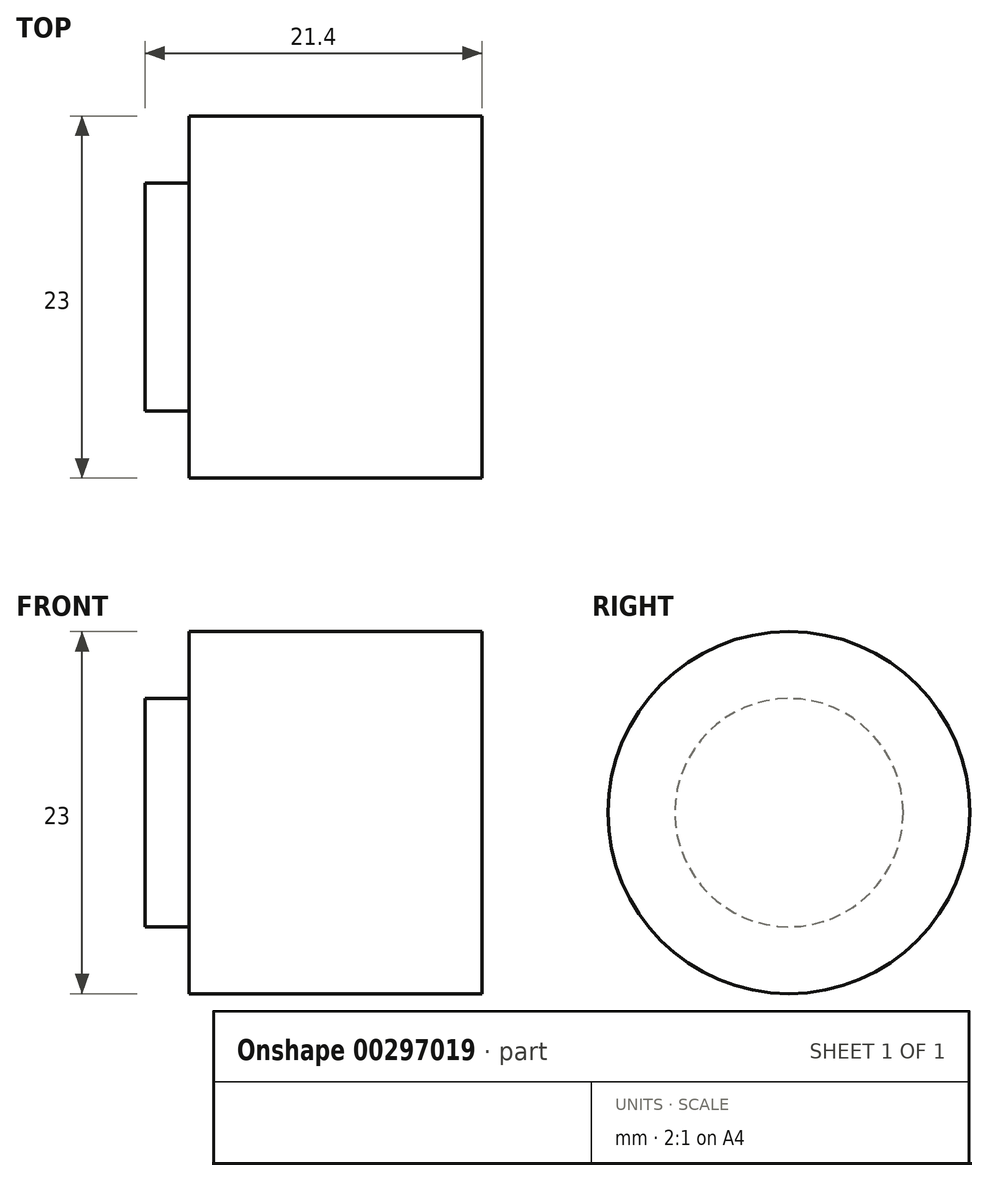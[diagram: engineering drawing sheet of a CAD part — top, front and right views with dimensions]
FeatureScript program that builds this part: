
annotation { "Feature Type Name" : "Feature", "Feature Type Description" : "" }
export const myFeature = defineFeature(function(context is Context, id is Id, definition is map)
    precondition{}
    {
        {
            var Q0;
            Q0=qCreatedBy(makeId("Front.planeOp"),FACE);
            var sketch = newSketch(context, id + "F0", { "sketchPlane" : qUnion([Q0])});
            skLineSegment(sketch, "E0.bottom", {"start": v(-18.6, 11.5) * mm, "end": v(0, 11.5) * mm});
            skLineSegment(sketch, "E0.top", {"start": v(-18.6, -11.5) * mm, "end": v(0, -11.5) * mm});
            skLineSegment(sketch, "E0.left", {"start": v(-18.6, 11.5) * mm, "end": v(-18.6, -11.5) * mm});
            skLineSegment(sketch, "E0.right", {"start": v(0, 11.5) * mm, "end": v(0, -11.5) * mm});
            skLineSegment(sketch, "E1.bottom", {"start": v(-21.4, -7.25) * mm, "end": v(-18.6, -7.25) * mm});
            skLineSegment(sketch, "E1.top", {"start": v(-21.4, 7.25) * mm, "end": v(-18.6, 7.25) * mm});
            skLineSegment(sketch, "E1.left", {"start": v(-21.4, 7.25) * mm, "end": v(-21.4, -7.25) * mm});
            skLineSegment(sketch, "E1.right", {"start": v(-18.6, 7.25) * mm, "end": v(-18.6, -7.25) * mm});
            skLineSegment(sketch, "E2", {"start": v(0, 0) * mm, "end": v(-21.4, 0) * mm});
            skSolve(sketch);
        }
        {
            var Q0;
            {var subQ1=sQuery(id+"F0.wireOp",EDGE,"E0.bottom");Q0=makeQuery(id+"F0.imprint","IMPRINT",FACE,{"disambiguationData":[TD([[makeQuery(id+"F0.imprint","IMPRINT",EDGE,{"derivedFrom":subQ1}),-1.0]])]});}
            var Q1;
            {var subQ0=sQuery(id+"F0.wireOp",EDGE,"E1.top");Q1=makeQuery(id+"F0.imprint","IMPRINT",FACE,{"disambiguationData":[TD([[makeQuery(id+"F0.imprint","IMPRINT",EDGE,{"derivedFrom":subQ0}),-1.0]])]});}
            var Q2;
            Q2=sQuery(id+"F0.wireOp",EDGE,"E2");
            revolve(context, id + "F1", {"entities" : qUnion([Q0, Q1]), "axis" : qUnion([Q2]), "revolveType" : RevolveType.FULL});
        }
    });
